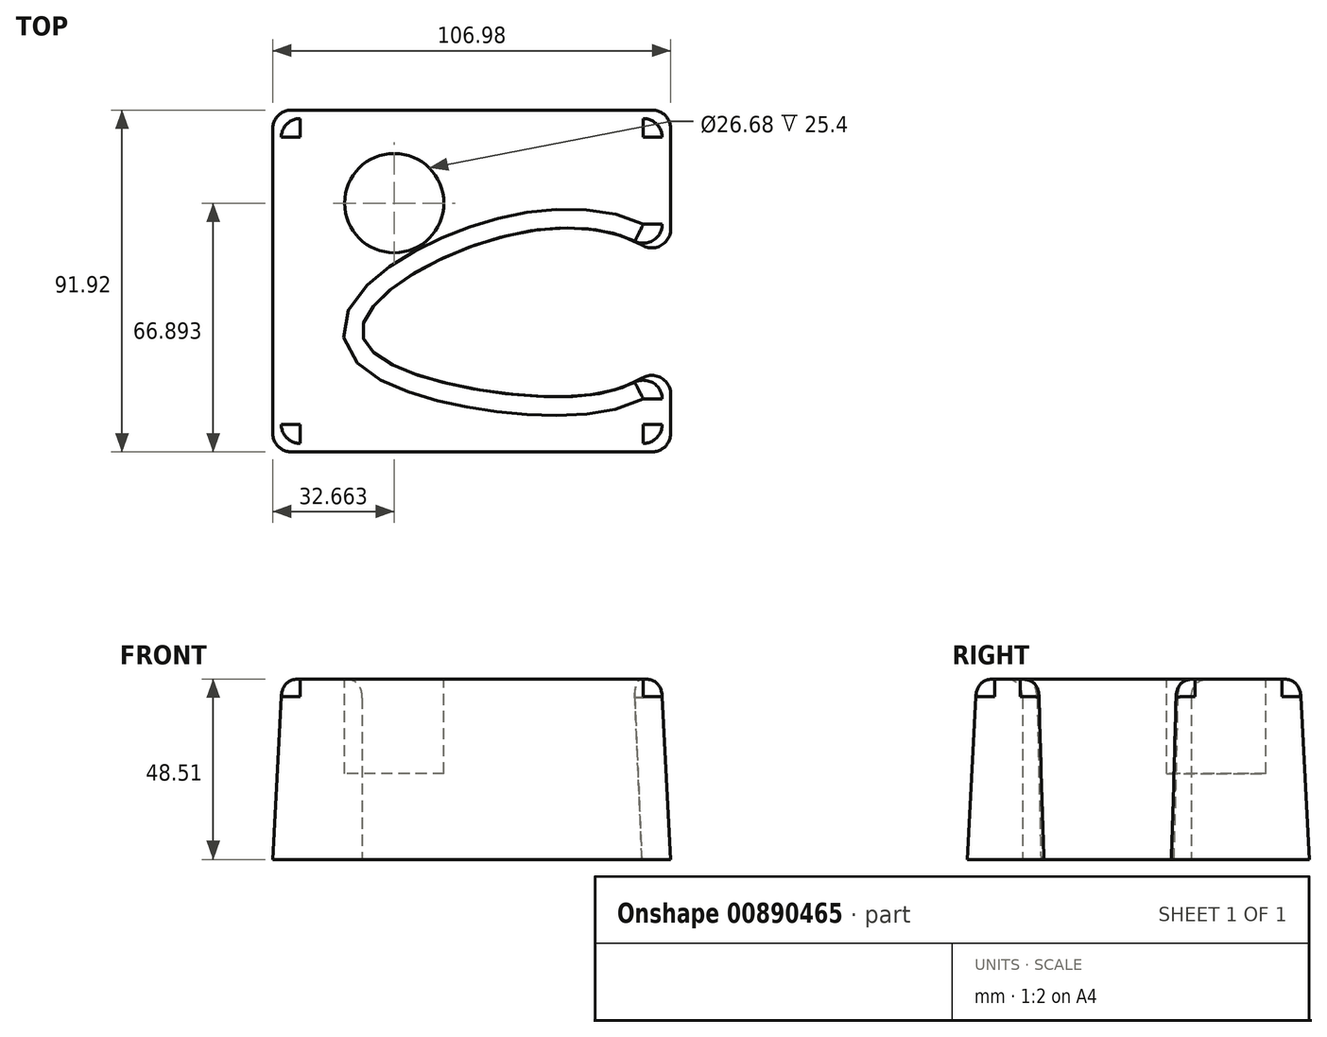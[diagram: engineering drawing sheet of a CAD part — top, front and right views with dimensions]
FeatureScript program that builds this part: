
annotation { "Feature Type Name" : "Feature", "Feature Type Description" : "" }
export const myFeature = defineFeature(function(context is Context, id is Id, definition is map)
    precondition{}
    {
        {
            var Q0;
            Q0=qCreatedBy(makeId("Top.planeOp"),FACE);
            var sketch = newSketch(context, id + "F0", { "sketchPlane" : qUnion([Q0])});
            skLineSegment(sketch, "E0.bottom", {"start": v(53.49, -45.96) * mm, "end": v(-53.49, -45.96) * mm});
            skLineSegment(sketch, "E0.top", {"start": v(53.49, 45.96) * mm, "end": v(-53.49, 45.96) * mm});
            skLineSegment(sketch, "E0.left", {"start": v(53.49, -45.96) * mm, "end": v(53.49, 45.96) * mm});
            skLineSegment(sketch, "E0.right", {"start": v(-53.49, -45.96) * mm, "end": v(-53.49, 45.96) * mm});
            skPoint(sketch, "E0.middle", {"position": v(0, 0) * mm});
            skSolve(sketch);
        }
        {
            var Q0;
            Q0 = qSketchRegion(id + "F0", true);
            extrude(context, id + "F1", {"entities" : qUnion([Q0]), "depth" : 48.5 * mm, "offsetDistance" : 25.4 * mm, "hasDraft" : true, "draftAngle" : 3 * degree, "draftPullDirection" : true});
        }
        {
            var Q0;
            Q0=makeQuery(id+"F1.opExtrude","CAP_FACE",FACE,{"disambiguationData":[OSD([sQuery(id+"F0.wireOp",EDGE,"E0.bottom"),sQuery(id+"F0.wireOp",EDGE,"E0.top"),sQuery(id+"F0.wireOp",EDGE,"E0.left"),sQuery(id+"F0.wireOp",EDGE,"E0.right")])],"isStart":false});
            var sketch = newSketch(context, id + "F2", { "sketchPlane" : qUnion([Q0])});
            skCircle(sketch, "E1", {"center": v(-20.83, 20.93) * mm, "radius": 13.34 * mm});
            skSolve(sketch);
        }
        {
            var Q0;
            Q0 = qSketchRegion(id + "F2", true);
            extrude(context, id + "F3", {"entities" : qUnion([Q0]), "operationType" : NewBodyOperationType.REMOVE, "oppositeDirection" : true, "depth" : 25.4 * mm, "offsetDistance" : 25.4 * mm});
        }
        {
            var Q0;
            Q0=makeQuery(id+"F1.opExtrude","SWEPT_EDGE",EDGE,{"disambiguationData":[OSD([sQuery(id+"F0.wireOp",EDGE,"E0.bottom"),sQuery(id+"F0.wireOp",EDGE,"E0.right")])]});
            var Q1;
            Q1=makeQuery(id+"F1.opExtrude","SWEPT_EDGE",EDGE,{"disambiguationData":[OSD([sQuery(id+"F0.wireOp",EDGE,"E0.bottom"),sQuery(id+"F0.wireOp",EDGE,"E0.left")])]});
            var Q2;
            Q2=makeQuery(id+"F1.opExtrude","SWEPT_EDGE",EDGE,{"disambiguationData":[OSD([sQuery(id+"F0.wireOp",EDGE,"E0.top"),sQuery(id+"F0.wireOp",EDGE,"E0.left")])]});
            var Q3;
            Q3=makeQuery(id+"F1.opExtrude","SWEPT_EDGE",EDGE,{"disambiguationData":[OSD([sQuery(id+"F0.wireOp",EDGE,"E0.top"),sQuery(id+"F0.wireOp",EDGE,"E0.right")])]});
            fillet(context, id + "F4", {"entities" : qUnion([Q0, Q1, Q2, Q3]), "radius" : 5.08 * mm, "tangentPropagation" : true, "allowEdgeOverflow" : false});
        }
        {
            var Q0;
            Q0=makeQuery(id+"F1.opExtrude","CAP_FACE",FACE,{"disambiguationData":[OSD([sQuery(id+"F0.wireOp",EDGE,"E0.bottom"),sQuery(id+"F0.wireOp",EDGE,"E0.top"),sQuery(id+"F0.wireOp",EDGE,"E0.left"),sQuery(id+"F0.wireOp",EDGE,"E0.right")])],"isStart":false});
            var sketch = newSketch(context, id + "F5", { "sketchPlane" : qUnion([Q0])});
            skFitSpline(sketch, "E2", {"points": [v(50.95, -21.36) * mm, v(13.57, -30.7) * mm, v(-29.35, -14.44) * mm, v(7.02, 11.59) * mm, v(50.95, 5.11) * mm, v(50.95, -21.36) * mm]});
            skSolve(sketch);
        }
        {
            var Q0;
            Q0 = qSketchRegion(id + "F5", true);
            extrude(context, id + "F6", {"entities" : qUnion([Q0]), "operationType" : NewBodyOperationType.REMOVE, "endBound" : BoundingType.THROUGH_ALL, "oppositeDirection" : true, "depth" : 25.4 * mm, "offsetDistance" : 25.4 * mm});
        }
        {
            var Q0;
            Q0=makeQuery(id+"F6.boolean.opBoolean","INTERSECT",EDGE,{"disambiguationData":[OD(0.0)],"derivedFrom":[makeQuery(id+"F1.opExtrude","SWEPT_FACE",FACE,{"disambiguationData":[OSD([sQuery(id+"F0.wireOp",EDGE,"E0.left")])]}),makeQuery(id+"F6.opExtrude","SWEPT_FACE",FACE,{"disambiguationData":[OSD([sQuery(id+"F5.wireOp",EDGE,"E2")])]})]});
            var Q1;
            Q1=makeQuery(id+"F6.boolean.opBoolean","INTERSECT",EDGE,{"disambiguationData":[OD(1.0)],"derivedFrom":[makeQuery(id+"F1.opExtrude","SWEPT_FACE",FACE,{"disambiguationData":[OSD([sQuery(id+"F0.wireOp",EDGE,"E0.left")])]}),makeQuery(id+"F6.opExtrude","SWEPT_FACE",FACE,{"disambiguationData":[OSD([sQuery(id+"F5.wireOp",EDGE,"E2")])]})]});
            fillet(context, id + "F7", {"entities" : qUnion([Q0, Q1]), "radius" : 5.08 * mm, "tangentPropagation" : true, "allowEdgeOverflow" : false});
        }
        {
            var Q0;
            Q0=makeQuery(id+"F1.opExtrude","CAP_EDGE",EDGE,{"disambiguationData":[OSD([sQuery(id+"F0.wireOp",EDGE,"E0.bottom")])],"isStart":false});
            fillet(context, id + "F8", {"entities" : qUnion([Q0]), "radius" : 5.08 * mm, "tangentPropagation" : true, "rho" : 0.5, "crossSection" : FilletCrossSection.CONIC, "allowEdgeOverflow" : false});
        }
    });
